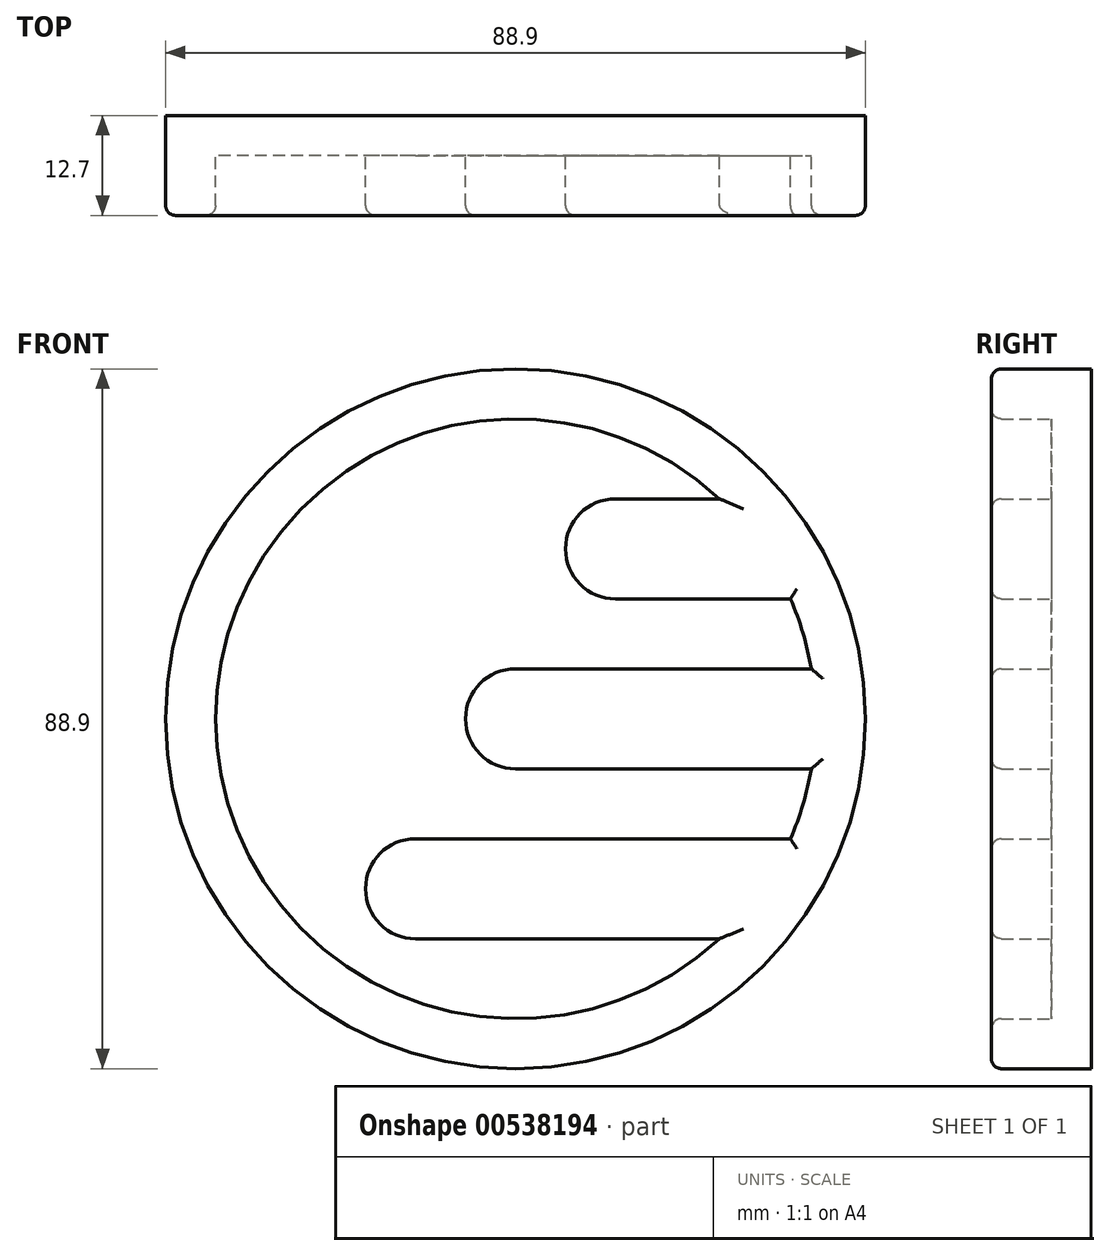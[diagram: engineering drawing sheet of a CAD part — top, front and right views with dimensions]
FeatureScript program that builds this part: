
annotation { "Feature Type Name" : "Feature", "Feature Type Description" : "" }
export const myFeature = defineFeature(function(context is Context, id is Id, definition is map)
    precondition{}
    {
        {
            var Q0;
            Q0=qCreatedBy(makeId("Front.planeOp"),FACE);
            var sketch = newSketch(context, id + "F0", { "sketchPlane" : qUnion([Q0])});
            skArc(sketch, "E0", {"start": v(25.9, 27.94) * mm, "mid": v(-38.1, 0) * mm, "end": v(25.9, -27.94) * mm});
            skLineSegment(sketch, "E1", {"start": v(0, 0) * mm, "end": v(0, -15.24) * mm});
            skLineSegment(sketch, "E2", {"start": v(0, -15.24) * mm, "end": v(-12.7, -15.24) * mm});
            skLineSegment(sketch, "E3", {"start": v(0, -27.94) * mm, "end": v(-12.7, -27.94) * mm});
            skArc(sketch, "E4", {"start": v(-12.7, -15.24) * mm, "mid": v(-19.05, -21.59) * mm, "end": v(-12.7, -27.94) * mm});
            skLineSegment(sketch, "E5", {"start": v(0, -27.94) * mm, "end": v(25.9, -27.94) * mm});
            skLineSegment(sketch, "E6", {"start": v(0, -15.24) * mm, "end": v(34.92, -15.24) * mm});
            skLineSegment(sketch, "E7", {"start": v(0, -6.35) * mm, "end": v(37.57, -6.35) * mm});
            skLineSegment(sketch, "E8", {"start": v(0, 6.35) * mm, "end": v(37.57, 6.35) * mm});
            skArc(sketch, "E9", {"start": v(0, 6.35) * mm, "mid": v(-6.35, 0) * mm, "end": v(0, -6.35) * mm});
            skLineSegment(sketch, "E10", {"start": v(12.7, 27.94) * mm, "end": v(25.9, 27.94) * mm});
            skLineSegment(sketch, "E11", {"start": v(12.7, 15.24) * mm, "end": v(34.92, 15.24) * mm});
            skArc(sketch, "E12", {"start": v(12.7, 27.94) * mm, "mid": v(6.35, 21.59) * mm, "end": v(12.7, 15.24) * mm});
            skPoint(sketch, "E12.midSnap0", {"position": v(12.7, 21.59) * mm});
            skPoint(sketch, "E12.midSnap1", {"position": v(6.35, 15.24) * mm});
            skCircle(sketch, "E13", {"center": v(0, 0) * mm, "radius": 44.45 * mm});
            skArc(sketch, "E14.trimOffspring", {"start": v(37.57, 6.35) * mm, "mid": v(36.51, 10.88) * mm, "end": v(34.92, 15.24) * mm});
            skArc(sketch, "E15.trimOffspring", {"start": v(34.92, -15.24) * mm, "mid": v(36.51, -10.88) * mm, "end": v(37.57, -6.35) * mm});
            skPoint(sketch, "E16.orphan", {"position": v(0, 15.24) * mm});
            skSolve(sketch);
        }
        {
            var Q0;
            Q0 = qSketchRegion(id + "F0", true);
            extrude(context, id + "F1", {"entities" : qUnion([Q0]), "depth" : 12.7 * mm, "offsetDistance" : 25.4 * mm});
        }
        {
            var Q0;
            Q0=qCreatedBy(makeId("Front.planeOp"),FACE);
            var sketch = newSketch(context, id + "F2", { "sketchPlane" : qUnion([Q0])});
            skCircle(sketch, "E17.0.0", {"center": v(0, 0) * mm, "radius": 44.45 * mm});
            skSolve(sketch);
        }
        {
            var Q0;
            Q0 = qSketchRegion(id + "F2", true);
            extrude(context, id + "F3", {"entities" : qUnion([Q0]), "operationType" : NewBodyOperationType.ADD, "depth" : 5.08 * mm, "offsetDistance" : 25.4 * mm});
        }
        {
            var Q0;
            Q0=makeQuery(id+"F1.opExtrude","CAP_EDGE",EDGE,{"disambiguationData":[OSD([sQuery(id+"F0.wireOp",EDGE,"E13")])],"isStart":false});
            var Q1;
            Q1=makeQuery(id+"F1.opExtrude","CAP_EDGE",EDGE,{"disambiguationData":[OSD([sQuery(id+"F0.wireOp",EDGE,"E3"),sQuery(id+"F0.wireOp",EDGE,"E5")])],"isStart":false});
            var Q2;
            Q2=makeQuery(id+"F1.opExtrude","CAP_EDGE",EDGE,{"disambiguationData":[OSD([sQuery(id+"F0.wireOp",EDGE,"E7")])],"isStart":false});
            var Q3;
            Q3=makeQuery(id+"F1.opExtrude","CAP_EDGE",EDGE,{"disambiguationData":[OSD([sQuery(id+"F0.wireOp",EDGE,"E11")])],"isStart":false});
            var Q4;
            Q4=makeQuery(id+"F1.opExtrude","CAP_EDGE",EDGE,{"disambiguationData":[OSD([sQuery(id+"F0.wireOp",EDGE,"E15.trimOffspring")])],"isStart":false});
            var Q5;
            Q5=makeQuery(id+"F1.opExtrude","CAP_EDGE",EDGE,{"disambiguationData":[OSD([sQuery(id+"F0.wireOp",EDGE,"E14.trimOffspring")])],"isStart":false});
            var Q6;
            Q6=makeQuery(id+"F1.opExtrude","CAP_EDGE",EDGE,{"disambiguationData":[OSD([sQuery(id+"F0.wireOp",EDGE,"E0")])],"isStart":false});
            fillet(context, id + "F4", {"entities" : qUnion([Q0, Q1, Q2, Q3, Q4, Q5, Q6]), "radius" : 1.27 * mm, "tangentPropagation" : true, "allowEdgeOverflow" : false});
        }
    });
